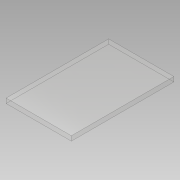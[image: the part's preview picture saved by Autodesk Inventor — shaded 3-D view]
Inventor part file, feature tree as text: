
AUTODESK INVENTOR PART (.ipt)
format: ipt  version: 2019 (Build 230136000, 136)  size: 80,896 bytes
history: native  units: mm
features: other x1, extrude x1, sketch x1
ambient origin geometry x8: Origin, YZ Plane, XZ Plane, XY Plane, X Axis, Y Axis, Z Axis, Center Point
bodies: Body1 (feature_tree)
feature tree (3):
  other  "Sólido1"
  extrude  "Extrusión1"  Depth=220.0mm
  sketch  "Boceto1"  dims[d0=140.0mm d1=220.0mm d2=10.0mm d3=0.0mm]
